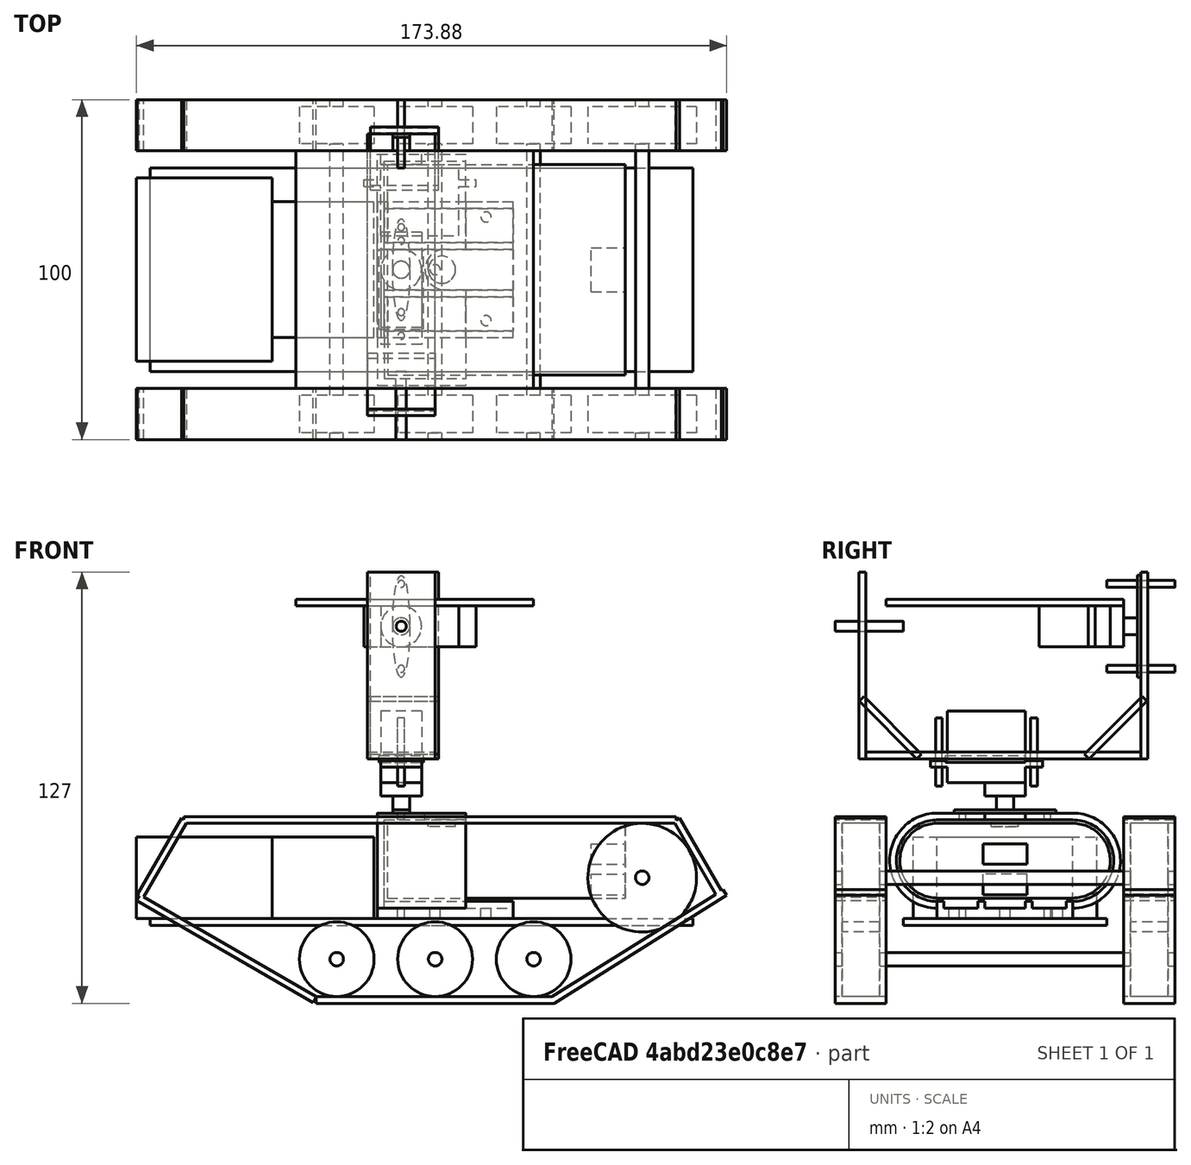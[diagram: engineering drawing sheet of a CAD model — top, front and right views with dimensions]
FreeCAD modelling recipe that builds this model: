
FCSTD DOCUMENT
Label: androidtank
License: CC-BY 3.0
LicenseURL: http://creativecommons.org/licenses/by/3.0/
objects: Part::Box×30, Part::Cylinder×30, Part::MultiFuse×17, Part::Cut×3, Part::FeaturePython×2, App::DocumentObjectGroup×1
note: 82 computed .brp shape members not serialized (recipe doc carries the construction recipe); baked Part::Feature solids carry a one-line shape summary decoded from their .brp

FEATURE [Part::Box] Box  label="MainFrame"
  Height = 2
  Length = 160
  Width = 60
FEATURE [Part::Box] Box001001  label="Moter Unit2"
  Height = 24
  Length = 30
  Placement = pos=(36,10,2) rot=(0,0,1;0rad)
  Width = 40
FEATURE [Part::Cylinder] Cylinder002  label="Wheel1"
  Angle = 360
  Height = 11
  Placement = pos=(20,-7,14) rot=(1,0,0;1.5708rad)
  Radius = 16
FEATURE [Part::Cylinder] Cylinder  label="Shaft"
  Angle = 360
  Height = 100
  Placement = pos=(20,-20,14) rot=(-1,0,0;1.5708rad)
  Radius = 2
FEATURE [Part::Cylinder] Cylinder002001  label="Wheel2"
  Angle = 360
  Height = 11
  Placement = pos=(20,78,14) rot=(1,0,0;1.5708rad)
  Radius = 16
FEATURE [Part::MultiFuse] Fusion001  label="WheelSet2"
  Placement = pos=(125,0,0) rot=(0,0,1;0rad)
  Shapes = -> [Cylinder,Cylinder002,Cylinder002001]
FEATURE [Part::Box] Box001002
  Height = 2
  Length = 145
  Placement = pos=(10,-20,30) rot=(0,0,1;0rad)
  Width = 15
FEATURE [Part::Box] Box001002001
  Height = 2
  Length = 70
  Placement = pos=(49,-20,-23) rot=(0,0,1;0rad)
  Width = 15
FEATURE [Part::Box] Box001002001001
  Height = 2
  Length = 60
  Placement = pos=(119,-20,-23) rot=(0,-1,0;0.558505rad)
  Width = 15
FEATURE [Part::Box] Box001002001002
  Height = 2
  Length = 60
  Placement = pos=(49,-20,-21) rot=(0,1,0;3.66519rad)
  Width = 15
FEATURE [Part::Box] Box001002001003
  Height = 2
  Length = 26
  Placement = pos=(-2,-20,8) rot=(0,-1,0;1.0472rad)
  Width = 15
FEATURE [Part::Box] Box001002001003001
  Height = 2
  Length = 26
  Placement = pos=(169,-20,9) rot=(0,-1,0;2.0944rad)
  Width = 15
FEATURE [Part::MultiFuse] Fusion002001002  label="Caterpiller1"
  Shapes = -> [Box001002,Box001002001,Box001002001002,Box001002001001,Box001002001003,Box001002001003001]
FEATURE [Part::MultiFuse] Fusion002001002001  label="Caterpiller2"
  Placement = pos=(0,85,0) rot=(0,0,1;0rad)
  Shapes = -> [Box001002,Box001002001,Box001002001002,Box001002001001,Box001002001003,Box001002001003001]
FEATURE [Part::Cylinder] Cylinder002001001002  label="Wheel006"
  Angle = 360
  Height = 11
  Placement = pos=(20,78,14) rot=(1,0,0;1.5708rad)
  Radius = 11
FEATURE [Part::Cylinder] Cylinder002001001002001  label="Wheel007"
  Angle = 360
  Height = 11
  Placement = pos=(20,-7,14) rot=(1,0,0;1.5708rad)
  Radius = 11
FEATURE [Part::Cylinder] Cylinder002001002001  label="Shaft002"
  Angle = 360
  Height = 100
  Placement = pos=(20,-20,14) rot=(-1,0,0;1.5708rad)
  Radius = 2
FEATURE [Part::MultiFuse] Fusion002001002002002  label="SWheelSet1"
  Placement = pos=(35,0,-24) rot=(0,0,1;0rad)
  Shapes = -> [Cylinder002001002001,Cylinder002001001002,Cylinder002001001002001]
FEATURE [Part::MultiFuse] Fusion002001002002002001  label="SWheelSet2"
  Placement = pos=(64,0,-24) rot=(0,0,1;0rad)
  Shapes = -> [Cylinder002001002001,Cylinder002001001002,Cylinder002001001002001]
FEATURE [Part::MultiFuse] Fusion002001002002002001001  label="SWheelSet3"
  Placement = pos=(93,0,-24) rot=(0,0,1;0rad)
  Shapes = -> [Cylinder002001002001,Cylinder002001001002,Cylinder002001001002001]
FEATURE [Part::Box] Box001002001003002
  Height = 22
  Length = 70
  Placement = pos=(0,0,-11) rot=(0,0,1;0rad)
  Width = 40
FEATURE [Part::Cylinder] Cylinder002001001002002
  Angle = 360
  Height = 70
  Placement = pos=(0,0,0) rot=(0,1,0;1.5708rad)
  Radius = 11
FEATURE [Part::Cylinder] Cylinder001
  Angle = 360
  Height = 70
  Placement = pos=(0,40,0) rot=(0,1,0;1.5708rad)
  Radius = 11
FEATURE [Part::Cylinder] Cylinder002001001002003  label="PowerButton"
  Angle = 360
  Height = 2
  Placement = pos=(16,20,10) rot=(0,0,1;0rad)
  Radius = 4
FEATURE [Part::Box] Box001002001003003  label="USB1"
  Height = 6
  Length = 15
  Placement = pos=(60,13.5,-1) rot=(0,0,1;0rad)
  Width = 13
FEATURE [Part::Box] Box001001001  label="USB2"
  Height = 6
  Length = 15
  Placement = pos=(60,13.5,-10) rot=(0,0,1;0rad)
  Width = 13
FEATURE [Part::MultiFuse] Fusion002001002002002001002
  Shapes = -> [Cylinder001,Box001002001003002,Cylinder002001001002002]
FEATURE [Part::MultiFuse] Fusion001001
  Shapes = -> [Box001001001,Cylinder002001001002003,Box001002001003003]
FEATURE [Part::Cut] Cut  label="Eneloop"
  Base = -> Fusion002001002002002001002
  Placement = pos=(70,10,19) rot=(0,0,1;0rad)
  Tool = -> Fusion001001
FEATURE [Part::Cylinder] Cylinder001001  label="Cylinder002"
  Angle = 360
  Height = 26
  Placement = pos=(0,50,19) rot=(0,1,0;1.5708rad)
  Radius = 14
FEATURE [Part::Box] Box001002001003002001  label="Box002"
  Height = 28
  Length = 26
  Placement = pos=(0,10,5) rot=(0,0,1;0rad)
  Width = 40
FEATURE [Part::Cylinder] Cylinder002001001002002001  label="Cylinder003"
  Angle = 360
  Height = 26
  Placement = pos=(0,10,19) rot=(0,1,0;1.5708rad)
  Radius = 14
FEATURE [Part::Box] Box001  label="Moter Unit1"
  Height = 24
  Length = 40
  Placement = pos=(-4,3,2) rot=(0,0,1;0rad)
  Width = 54
FEATURE [App::DocumentObjectGroup] ____________  label="DriveFrame"
  Group = -> [Box,Box001,Box001001,Fusion002001002,Fusion002001002001,Fusion002001002002002,Fusion002001002002002001,Fusion002001002002002001001,Fusion001]
FEATURE [Part::Box] Box001002001003002001001  label="Box003"
  Height = 5
  Length = 40
  Placement = pos=(0,10,2) rot=(0,0,1;0rad)
  Width = 40
FEATURE [Part::Box] Box001002001003002001002  label="Box004"
  Height = 24
  Length = 26
  Placement = pos=(2,10,7) rot=(0,0,1;0rad)
  Width = 40
FEATURE [Part::Cylinder] Cylinder001001001  label="Cylinder004"
  Angle = 360
  Height = 26
  Placement = pos=(2,50,19) rot=(0,1,0;1.5708rad)
  Radius = 12
FEATURE [Part::Cylinder] Cylinder002001001002002001001  label="Cylinder005"
  Angle = 360
  Height = 26
  Placement = pos=(2,10,19) rot=(0,1,0;1.5708rad)
  Radius = 12
FEATURE [Part::Cylinder] Cylinder002001001002003001  label="PowerButton001"
  Angle = 360
  Height = 4
  Placement = pos=(20,30,30) rot=(0,0,1;0rad)
  Radius = 6
FEATURE [Part::Box] Box001002001003002001003  label="Box005"
  Height = 4
  Length = 10
  Placement = pos=(20,24,30) rot=(0,0,1;0rad)
  Width = 12
FEATURE [Part::Box] Box001002001003002001001001  label="Box006"
  Height = 3
  Length = 40
  Placement = pos=(2,12,5) rot=(0,0,1;0rad)
  Width = 10
FEATURE [Part::Box] Box001002001003002001001001001  label="Box007"
  Height = 3
  Length = 40
  Placement = pos=(2,24,5) rot=(0,0,1;0rad)
  Width = 12
FEATURE [Part::Box] Box001002001003002001001001001001  label="Box008"
  Height = 3
  Length = 40
  Placement = pos=(2,38,5) rot=(0,0,1;0rad)
  Width = 10
FEATURE [Part::MultiFuse] Fusion002001002002002001003
  Shapes = -> [Box001002001003002001,Cylinder001001,Cylinder002001001002002001,Box001002001003002001001]
FEATURE [Part::MultiFuse] Fusion002001002002002001004
  Shapes = -> [Box001002001003002001002,Cylinder002001001002002001001,Cylinder001001001,Box001002001003002001001001001001,Box001002001003002001001001001,Box001002001003002001001001,Box001002001003002001003,Cylinder002001001002003001]
FEATURE [Part::Cut] Cut001  label="BatteryFrame"
  Base = -> Fusion002001002002002001003
  Placement = pos=(67,0,0) rot=(0,0,1;0rad)
  Tool = -> Fusion002001002002002001004
FEATURE [Part::Cylinder] Cylinder002001001002002001002001  label="Cylinder007"
  Angle = 360
  Height = 40
  Placement = pos=(74,17.5,0) rot=(0,0,1;0rad)
  Radius = 1
FEATURE [Part::Cylinder] Cylinder002001001002002001002  label="Cylinder006"
  Angle = 360
  Height = 40
  Placement = pos=(74,42.5,0) rot=(0,0,1;0rad)
  Radius = 1
FEATURE [Part::Cylinder] Cylinder002001001002002001002001001  label="Cylinder008"
  Angle = 360
  Height = 40
  Placement = pos=(84,30,0) rot=(0,0,1;0rad)
  Radius = 1.5
FEATURE [Part::Cylinder] Cylinder002001001002002001002001002  label="Cylinder009"
  Angle = 360
  Height = 40
  Placement = pos=(99,45.5,0) rot=(0,0,1;0rad)
  Radius = 1.5
FEATURE [Part::Cylinder] Cylinder002001001002002001002001003  label="Cylinder0010"
  Angle = 360
  Height = 40
  Placement = pos=(99,15,0) rot=(0,0,1;0rad)
  Radius = 1.5
FEATURE [Part::MultiFuse] Fusion002001002002002001005  label="BatteryFrameHoles"
  Shapes = -> [Cylinder002001001002002001002001,Cylinder002001001002002001002,Cylinder002001001002002001002001003,Cylinder002001001002002001002001002,Cylinder002001001002002001002001001]
FEATURE [Part::Cut] Cut002  label="BatteryFrame2"
  Base = -> Cut001
  Tool = -> Fusion002001002002002001005
FEATURE [Part::Box] Box001002001003002001001001001002  label="ServoBody"
  Height = 21
  Length = 23
  Width = 12
FEATURE [Part::Cylinder] Cylinder002001001002002001002001004  label="ServoBody2"
  Angle = 360
  Height = 4
  Placement = pos=(6,6,21) rot=(0,0,1;0rad)
  Radius = 6
FEATURE [Part::Box] Box001002001003002001001001001003  label="ServoBody3"
  Height = 2
  Length = 33
  Placement = pos=(-5,0,14.5) rot=(0,0,1;0rad)
  Width = 12
FEATURE [Part::Cylinder] Cylinder001001002  label="ServoAxis"
  Angle = 360
  Height = 4
  Placement = pos=(6,6,24) rot=(0,0,1;0rad)
  Radius = 2.5
FEATURE [Part::MultiFuse] Fusion005  label="ServoArmL"
  Shapes = -> [Cylinder001001002,Box001002001003002001001001001003,Box001002001003002001001001001002,Cylinder002001001002002001002001004]
FEATURE [Part::Cylinder] Cylinder002001001002002001002001005
  Angle = 360
  Height = 2
  Radius = 2.5
FEATURE [Part::FeaturePython] Scale  # Draft clone (typed FeaturePython)
  Objects = -> [Cylinder002001001002002001002001005]
  Placement = pos=(0,0,1) rot=(0,0,1;0rad)
  Scale = (6,1,0.5)
FEATURE [Part::MultiFuse] Fusion  label="Arm"
  Placement = pos=(6,6,28) rot=(0,0,1;0rad)
  Shapes = -> [Cylinder002001001002002001002001005,Scale]
FEATURE [Part::MultiFuse] Fusion006  label="ServoYaw"
  Placement = pos=(80,36,63) rot=(0.707107,-0.707107,0;3.14159rad)
  Shapes = -> [Fusion005,Fusion]
FEATURE [Part::Box] Box001002001003002001001001001004  label="ServoBody004"
  Height = 21
  Length = 23
  Width = 12
FEATURE [Part::Cylinder] Cylinder002001001002002001002001006  label="ServoBody005"
  Angle = 360
  Height = 4
  Placement = pos=(6,6,21) rot=(0,0,1;0rad)
  Radius = 6
FEATURE [Part::Box] Box001002001003002001001001001005  label="ServoBody006"
  Height = 2
  Length = 33
  Placement = pos=(-5,0,14.5) rot=(0,0,1;0rad)
  Width = 12
FEATURE [Part::Cylinder] Cylinder001001003  label="ServoAxis001"
  Angle = 360
  Height = 4
  Placement = pos=(6,6,24) rot=(0,0,1;0rad)
  Radius = 2.5
FEATURE [Part::MultiFuse] Fusion005001  label="ServoArmL001"
  Shapes = -> [Cylinder001001003,Box001002001003002001001001001005,Box001002001003002001001001001004,Cylinder002001001002002001002001006]
FEATURE [Part::Cylinder] Cylinder002001001002002001002001007
  Angle = 360
  Height = 2
  Radius = 2.5
FEATURE [Part::FeaturePython] Scale001  # Draft clone (typed FeaturePython)
  Objects = -> [Cylinder002001001002002001002001007]
  Placement = pos=(0,0,1) rot=(0,0,1;0rad)
  Scale = (6,1,0.5)
FEATURE [Part::MultiFuse] Fusion002001002002002001006  label="Arm001"
  Placement = pos=(6,6,28) rot=(0,0,1;1.5708rad)
  Shapes = -> [Cylinder002001001002002001002001007,Scale001]
FEATURE [Part::MultiFuse] Fusion006001  label="ServoPitch"
  Placement = pos=(68,40,94) rot=(-1,0,0;1.5708rad)
  Shapes = -> [Fusion005001,Fusion002001002002002001006]
FEATURE [Part::Box] Box001002001003002001001001001006  label="Box009"
  Height = 2
  Length = 70
  Placement = pos=(43,-5,94) rot=(0,0,1;0rad)
  Width = 70
FEATURE [Part::Box] Box001002001003002001001001001006001  label="Box010"
  Height = 55
  Length = 20
  Placement = pos=(65,70,49) rot=(0,0,1;0rad)
  Width = 2
FEATURE [Part::Box] Box001002001003002001001001001006001001  label="Box011"
  Height = 2
  Length = 13
  Placement = pos=(67.5,12.5,48) rot=(0,0,1;0rad)
  Width = 23.5
FEATURE [Part::Box] Box001002001003002001001001001006001001001  label="Box012"
  Height = 55
  Length = 20
  Placement = pos=(64,-13,49) rot=(0,0,1;0rad)
  Width = 2
FEATURE [Part::Cylinder] Cylinder002001001002002001002001008  label="Hole1"
  Angle = 360
  Height = 20
  Placement = pos=(74,-20,88) rot=(-1,0,0;1.5708rad)
  Radius = 1.5
FEATURE [Part::Cylinder] Cylinder002001001002002001002001008001  label="Hole2"
  Angle = 360
  Height = 20
  Placement = pos=(74,60,100.5) rot=(-1,0,0;1.5708rad)
  Radius = 1
FEATURE [Part::Cylinder] Cylinder002001001002002001002001008001001  label="Hole4"
  Angle = 360
  Height = 20
  Placement = pos=(74,38.5,41) rot=(0,0,1;0rad)
  Radius = 1
FEATURE [Part::Box] Box001002001003002001001001001006001001002  label="Box001002001003003"
  Height = 2
  Length = 20
  Placement = pos=(64,-11,49) rot=(0,0,1;0rad)
  Width = 81
FEATURE [Part::Cylinder] Cylinder002001001002002001002001008001001001  label="Hole3"
  Angle = 360
  Height = 20
  Placement = pos=(74,60,75.5) rot=(-1,0,0;1.5708rad)
  Radius = 1
FEATURE [Part::Cylinder] Cylinder002001001002002001002001008001001002  label="Hole5"
  Angle = 360
  Height = 20
  Placement = pos=(74,10.5,41) rot=(0,0,1;0rad)
  Radius = 1
FEATURE [Part::Box] Box001002001003002001001001001006001001001001  label="Box013"
  Height = 24
  Length = 20
  Placement = pos=(64,4,49) rot=(1,0,0;0.785397rad)
  Width = 2
FEATURE [Part::Box] Box001002001003002001001001001006001001001001001  label="Box014"
  Height = 24
  Length = 20
  Placement = pos=(65,53.41,50.41) rot=(-1,0,0;0.785397rad)
  Width = 2
